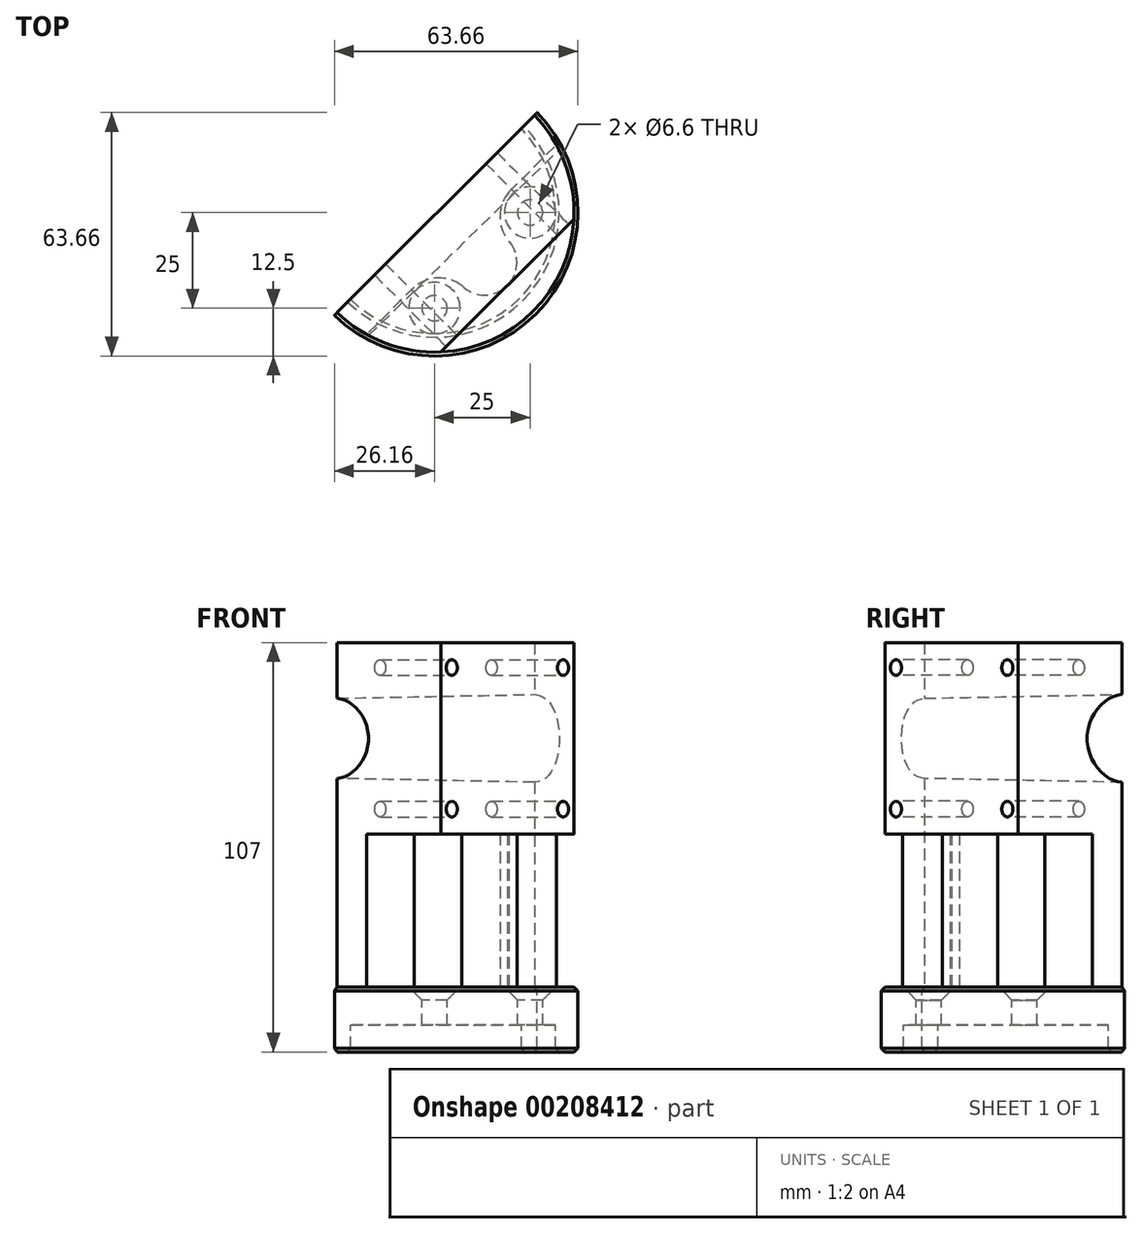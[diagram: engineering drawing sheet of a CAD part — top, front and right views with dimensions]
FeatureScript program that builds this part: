
annotation { "Feature Type Name" : "Feature", "Feature Type Description" : "" }
export const myFeature = defineFeature(function(context is Context, id is Id, definition is map)
    precondition{}
    {
        {
            var Q0;
            Q0=qCreatedBy(makeId("Front.planeOp"),FACE);
            var sketch = newSketch(context, id + "F0", { "sketchPlane" : qUnion([Q0])});
            skLineSegment(sketch, "E0", {"start": v(0, 0) * mm, "end": v(31.6, 0) * mm});
            skLineSegment(sketch, "E1", {"start": v(31.6, 0) * mm, "end": v(31.6, -7) * mm});
            skLineSegment(sketch, "E2", {"start": v(31.6, -7) * mm, "end": v(37.5, -7) * mm});
            skLineSegment(sketch, "E3", {"start": v(37.5, -7) * mm, "end": v(37.5, 10) * mm});
            skLineSegment(sketch, "E4", {"start": v(37.5, 10) * mm, "end": v(0, 10) * mm});
            skLineSegment(sketch, "E5", {"start": v(0, 10) * mm, "end": v(0, 0) * mm});
            skSolve(sketch);
        }
        {
            var Q0;
            Q0=qSketchRegion(id+"F0",true);
            var Q1;
            Q1=sQuery(id+"F0.wireOp",EDGE,"E5");
            revolve(context, id + "F1", {"entities" : qUnion([Q0]), "axis" : qUnion([Q1]), "revolveType" : RevolveType.TWO_DIRECTIONS, "angle" : 135 * degree, "angleBack" : 315 * degree});
        }
        {
            var Q0;
            Q0=makeQuery(id+"F1.opRevolve","SWEPT_EDGE",EDGE,{"disambiguationData":[OSD([sQuery(id+"F0.wireOp",EDGE,"E1"),sQuery(id+"F0.wireOp",EDGE,"E2")])]});
            var Q1;
            Q1=makeQuery(id+"F1.opRevolve","SWEPT_EDGE",EDGE,{"disambiguationData":[OSD([sQuery(id+"F0.wireOp",EDGE,"E2"),sQuery(id+"F0.wireOp",EDGE,"E3")])]});
            var Q2;
            Q2=makeQuery(id+"F1.opRevolve","SWEPT_EDGE",EDGE,{"disambiguationData":[OSD([sQuery(id+"F0.wireOp",EDGE,"E3"),sQuery(id+"F0.wireOp",EDGE,"E4")])]});
            chamfer(context, id + "F2", {"entities" : qUnion([Q0, Q1, Q2]), "width" : 1 * mm, "tangentPropagation" : true});
        }
        {
            var Q0;
            Q0=makeQuery(id+"F1.opRevolve","SWEPT_FACE",FACE,{"disambiguationData":[OSD([sQuery(id+"F0.wireOp",EDGE,"E4")])]});
            var sketch = newSketch(context, id + "F3", { "sketchPlane" : qUnion([Q0])});
            skCircle(sketch, "E6", {"center": v(0, 0) * mm, "radius": 25 * mm, "construction": true});
            skPoint(sketch, "E7", {"position": v(25, 0) * mm});
            skPoint(sketch, "E8", {"position": v(0, -25) * mm});
            skSolve(sketch);
        }
        {
            var Q0;
            Q0=sQuery(id+"F3.wireOp",VERTEX,"06cf2421-47d0-4dc6-992a-3eddbef67247");
            var Q1;
            Q1=sQuery(id+"F3.wireOp",VERTEX,"E7");
            var Q2;
            Q2=sQuery(id+"F3.wireOp",VERTEX,"E8");
            var Q3;
            Q3=sQuery(id+"F3.wireOp",VERTEX,"fbc0e9e7-8500-45a9-a549-826aceaf9aa4");
            var Q4;
            Q4=makeQuery(id+"F1.opRevolve","SWEPT_BODY",BODY,{"disambiguationData":[OSD([sQuery(id+"F0.wireOp",EDGE,"E0"),sQuery(id+"F0.wireOp",EDGE,"E1"),sQuery(id+"F0.wireOp",EDGE,"E2"),sQuery(id+"F0.wireOp",EDGE,"E3"),sQuery(id+"F0.wireOp",EDGE,"E4"),sQuery(id+"F0.wireOp",EDGE,"E5")])]});
            hole(context, id + "F4", {"style" : HoleStyle.C_SINK, "endStyle" : HoleEndStyle.THROUGH, "standardTappedOrClearance" : lookupTablePath({ "standard" : "ISO", "fit" : "Normal", "size" : "M6", "type" : "Clearance" }), "standardBlindInLast" : lookupTablePath({ "fit" : "Standard", "standard" : "ISO", "size" : "M6", "type" : "Clearance" }), "holeDiameter" : 6.6 * mm, "cSinkDiameter" : 13.44 * mm, "cSinkAngle" : 90 * degree, "locations" : qUnion([Q0, Q1, Q2, Q3]), "scope" : qUnion([Q4]), "isTappedThrough" : true});
        }
        {
            var Q0;
            Q0=makeQuery(id+"F1.opRevolve","SWEPT_FACE",FACE,{"disambiguationData":[OSD([sQuery(id+"F0.wireOp",EDGE,"E4")])]});
            var sketch = newSketch(context, id + "F5", { "sketchPlane" : qUnion([Q0])});
            skLineSegment(sketch, "E9", {"start": v(0, 0) * mm, "end": v(7.07, -7.07) * mm});
            skLineSegment(sketch, "E10", {"start": v(7.07, -7.07) * mm, "end": v(31.9, 17.75) * mm});
            skLineSegment(sketch, "E11", {"start": v(7.07, -7.07) * mm, "end": v(-17.75, -31.9) * mm});
            skLineSegment(sketch, "E12.bottom", {"start": v(7.07, -7.07) * mm, "end": v(19.07, -7.07) * mm, "construction": true});
            skLineSegment(sketch, "E12.top", {"start": v(7.07, -19.07) * mm, "end": v(19.07, -19.07) * mm, "construction": true});
            skLineSegment(sketch, "E12.left", {"start": v(7.07, -7.07) * mm, "end": v(7.07, -19.07) * mm, "construction": true});
            skLineSegment(sketch, "E12.right", {"start": v(19.07, -7.07) * mm, "end": v(19.07, -19.07) * mm, "construction": true});
            skArc(sketch, "E13", {"start": v(7.07, -19.07) * mm, "mid": v(0.8, -17.12) * mm, "end": v(-5.34, -19.48) * mm});
            skArc(sketch, "E14", {"start": v(19.48, 5.34) * mm, "mid": v(17.12, -0.8) * mm, "end": v(19.07, -7.07) * mm});
            skArc(sketch, "E15", {"start": v(7.07, -19.07) * mm, "mid": v(19.07, -19.07) * mm, "end": v(19.07, -7.07) * mm});
            skSolve(sketch);
        }
        {
            var Q0;
            Q0=qSketchRegion(id+"F5",true);
            var Q1;
            {var subQ7=sQuery(id+"F5.wireOp",EDGE,"E9");Q1=makeQuery(id+"F5.imprint","IMPRINT",FACE,{"disambiguationData":[TD([[makeQuery(id+"F5.imprint","IMPRINT",EDGE,{"derivedFrom":subQ7}),-1.0]])]});}
            var Q2;
            {var subQ6=sQuery(id+"F5.wireOp",EDGE,"E9");Q2=makeQuery(id+"F5.imprint","IMPRINT",FACE,{"disambiguationData":[TD([[makeQuery(id+"F5.imprint","IMPRINT",EDGE,{"derivedFrom":subQ6}),1.0]])]});}
            extrude(context, id + "F6", {"entities" : qUnion([Q0, Q1, Q2]), "operationType" : NewBodyOperationType.ADD, "depth" : 40 * mm});
        }
        {
            var Q0;
            Q0=makeQuery(id+"F6.opExtrude","CAP_FACE",FACE,{"disambiguationData":[OSD([sQuery(id+"F0.wireOp",EDGE,"E3"),sQuery(id+"F0.wireOp",EDGE,"E4"),sQuery(id+"F5.wireOp",EDGE,"E10"),sQuery(id+"F5.wireOp",EDGE,"E11"),sQuery(id+"F5.wireOp",EDGE,"E13"),sQuery(id+"F5.wireOp",EDGE,"E14"),sQuery(id+"F5.wireOp",EDGE,"E15")])],"isStart":false});
            var sketch = newSketch(context, id + "F7", { "sketchPlane" : qUnion([Q0])});
            skArc(sketch, "E16", {"start": v(25.8, 25.8) * mm, "mid": v(25.8, -25.8) * mm, "end": v(-25.8, -25.8) * mm});
            skLineSegment(sketch, "E17", {"start": v(-25.8, -25.8) * mm, "end": v(25.8, 25.8) * mm});
            skLineSegment(sketch, "E18", {"start": v(19.07, -19.07) * mm, "end": v(36.46, -1.68) * mm});
            skLineSegment(sketch, "E19", {"start": v(36.46, -1.68) * mm, "end": v(1.68, -36.46) * mm});
            skSolve(sketch);
        }
        {
            var Q0;
            {var subQ1=makeQuery(id+"F6.opExtrude","CAP_EDGE",EDGE,{"disambiguationData":[OSD([sQuery(id+"F5.wireOp",EDGE,"E10")])],"isStart":false});Q0=makeQuery(id+"F7.imprint","IMPRINT",FACE,{"disambiguationData":[TD([[makeQuery(id+"F7.imprint","IMPRINT",EDGE,{"derivedFrom":subQ1}),-1.0]])]});}
            var Q1;
            {var subQ1=makeQuery(id+"F6.opExtrude","CAP_EDGE",EDGE,{"disambiguationData":[OSD([sQuery(id+"F5.wireOp",EDGE,"E11")])],"isStart":false});Q1=makeQuery(id+"F7.imprint","IMPRINT",FACE,{"disambiguationData":[TD([[makeQuery(id+"F7.imprint","IMPRINT",EDGE,{"derivedFrom":subQ1}),1.0]])]});}
            var Q2;
            {var subQ0=sQuery(id+"F7.wireOp",EDGE,"E17");Q2=makeQuery(id+"F7.imprint","IMPRINT",FACE,{"disambiguationData":[TD([[makeQuery(id+"F7.imprint","IMPRINT",EDGE,{"derivedFrom":subQ0}),-1.0]])]});}
            extrude(context, id + "F8", {"entities" : qUnion([Q0, Q1, Q2]), "operationType" : NewBodyOperationType.ADD, "depth" : 50 * mm});
        }
        {
            var Q0;
            {var subQ0=sQuery(id+"F0.wireOp",EDGE,"E4");Q0=makeQuery(id+"F8.boolean.opBoolean","MERGE",FACE,{"derivedFrom":[makeQuery(id+"F6.boolean.opBoolean","MERGE",FACE,{"derivedFrom":[makeQuery(id+"F1.opRevolve","CAP_FACE",FACE,{"disambiguationData":[OSD([sQuery(id+"F0.wireOp",EDGE,"E0"),sQuery(id+"F0.wireOp",EDGE,"E1"),sQuery(id+"F0.wireOp",EDGE,"E2"),sQuery(id+"F0.wireOp",EDGE,"E3"),subQ0,sQuery(id+"F0.wireOp",EDGE,"E5")])],"isStart":true}),makeQuery(id+"F6.opExtrude","SWEPT_FACE",FACE,{"disambiguationData":[OSD([subQ0])]})]}),makeQuery(id+"F8.opExtrude","SWEPT_FACE",FACE,{"disambiguationData":[OSD([sQuery(id+"F7.wireOp",EDGE,"E17")])]})]});}
            var sketch = newSketch(context, id + "F9", { "sketchPlane" : qUnion([Q0])});
            skLineSegment(sketch, "E20", {"start": v(-36.5, 100) * mm, "end": v(-36.5, 86.5) * mm, "construction": true});
            skLineSegment(sketch, "E21", {"start": v(36.5, 100) * mm, "end": v(36.5, 85.5) * mm, "construction": true});
            skLineSegment(sketch, "E22", {"start": v(-36.5, 86.5) * mm, "end": v(-36.5, 63.5) * mm, "construction": true});
            skLineSegment(sketch, "E23", {"start": v(36.5, 85.5) * mm, "end": v(36.5, 64.5) * mm, "construction": true});
            skLineSegment(sketch, "E24", {"start": v(-36.5, 86.5) * mm, "end": v(36.5, 85.5) * mm});
            skLineSegment(sketch, "E25", {"start": v(36.5, 85.5) * mm, "end": v(36.5, 64.5) * mm});
            skLineSegment(sketch, "E26", {"start": v(36.5, 64.5) * mm, "end": v(-36.5, 63.5) * mm});
            skLineSegment(sketch, "E27", {"start": v(-36.5, 63.5) * mm, "end": v(-36.5, 86.5) * mm});
            skLineSegment(sketch, "E28", {"start": v(-36.5, 75) * mm, "end": v(36.5, 75) * mm});
            skSolve(sketch);
        }
        {
            var Q0;
            {var subQ0=sQuery(id+"F9.wireOp",EDGE,"E24");Q0=makeQuery(id+"F9.imprint","IMPRINT",FACE,{"disambiguationData":[TD([[makeQuery(id+"F9.imprint","IMPRINT",EDGE,{"derivedFrom":subQ0}),-1.0]])]});}
            var Q1;
            Q1=sQuery(id+"F9.wireOp",EDGE,"E28");
            revolve(context, id + "F10", {"operationType" : NewBodyOperationType.REMOVE, "entities" : qUnion([Q0]), "axis" : qUnion([Q1]), "revolveType" : RevolveType.FULL, "oppositeDirection" : true});
        }
        {
            var Q0;
            Q0=makeQuery(id+"F8.opExtrude","SWEPT_FACE",FACE,{"disambiguationData":[OSD([sQuery(id+"F7.wireOp",EDGE,"E19")])]});
            var sketch = newSketch(context, id + "F11", { "sketchPlane" : qUnion([Q0])});
            skLineSegment(sketch, "E29", {"start": v(24.6, 100) * mm, "end": v(24.6, 93.5) * mm, "construction": true});
            skLineSegment(sketch, "E30", {"start": v(24.6, 93.5) * mm, "end": v(20.6, 93.5) * mm, "construction": true});
            skLineSegment(sketch, "E31", {"start": v(-24.6, 100) * mm, "end": v(-24.6, 93.5) * mm, "construction": true});
            skLineSegment(sketch, "E32", {"start": v(-24.6, 93.5) * mm, "end": v(-20.6, 93.5) * mm, "construction": true});
            skLineSegment(sketch, "E33", {"start": v(-24.6, 50) * mm, "end": v(-24.6, 56.5) * mm, "construction": true});
            skLineSegment(sketch, "E34", {"start": v(-24.6, 56.5) * mm, "end": v(-20.6, 56.5) * mm, "construction": true});
            skLineSegment(sketch, "E35", {"start": v(24.6, 50) * mm, "end": v(24.6, 56.5) * mm, "construction": true});
            skLineSegment(sketch, "E36", {"start": v(24.6, 56.5) * mm, "end": v(20.6, 56.5) * mm, "construction": true});
            skPoint(sketch, "E37", {"position": v(-20.6, 93.5) * mm});
            skPoint(sketch, "E38", {"position": v(20.6, 93.5) * mm});
            skPoint(sketch, "E39", {"position": v(20.6, 56.5) * mm});
            skPoint(sketch, "E40", {"position": v(-20.6, 56.5) * mm});
            skSolve(sketch);
        }
        {
            var Q0;
            Q0=sQuery(id+"F11.wireOp",VERTEX,"E38");
            var Q1;
            Q1=sQuery(id+"F11.wireOp",VERTEX,"E39");
            var Q2;
            Q2=sQuery(id+"F11.wireOp",VERTEX,"E40");
            var Q3;
            Q3=sQuery(id+"F11.wireOp",VERTEX,"E37");
            var Q4;
            Q4=makeQuery(id+"F1.opRevolve","SWEPT_BODY",BODY,{"disambiguationData":[OSD([sQuery(id+"F0.wireOp",EDGE,"E0"),sQuery(id+"F0.wireOp",EDGE,"E1"),sQuery(id+"F0.wireOp",EDGE,"E2"),sQuery(id+"F0.wireOp",EDGE,"E3"),sQuery(id+"F0.wireOp",EDGE,"E4"),sQuery(id+"F0.wireOp",EDGE,"E5")])]});
            hole(context, id + "F12", {"style" : HoleStyle.SIMPLE, "endStyle" : HoleEndStyle.THROUGH, "standardTappedOrClearance" : lookupTablePath({ "standard" : "ISO", "engagement" : "75%", "pitch" : "0.9 mm", "size" : "M5", "type" : "Tapped" }), "standardBlindInLast" : lookupTablePath({ "standard" : "ISO", "engagement" : "75%", "pitch" : "0.9 mm", "size" : "M5", "type" : "Tapped" }), "holeDiameter" : 4.1 * mm, "startFromSketch" : true, "locations" : qUnion([Q0, Q1, Q2, Q3]), "scope" : qUnion([Q4]), "isTappedThrough" : true, "showTappedDepth" : true});
        }
        {
            var Q0;
            {var subQ0=sQuery(id+"F0.wireOp",EDGE,"E4");var subQ1=sQuery(id+"F0.wireOp",EDGE,"E3");var subQ2=sQuery(id+"F7.wireOp",EDGE,"E17");var subQ7=sQuery(id+"F0.wireOp",EDGE,"E2");var subQ8=sQuery(id+"F0.wireOp",EDGE,"E1");var subQ9=sQuery(id+"F0.wireOp",EDGE,"E0");Q0=makeQuery(id+"F10.boolean.opBoolean","SPLIT",FACE,{"disambiguationData":[TD([makeQuery(id+"F1.opRevolve","SWEPT_FACE",FACE,{"disambiguationData":[OSD([subQ9])]})])],"derivedFrom":makeQuery(id+"F8.boolean.opBoolean","MERGE",FACE,{"derivedFrom":[makeQuery(id+"F6.boolean.opBoolean","MERGE",FACE,{"derivedFrom":[makeQuery(id+"F1.opRevolve","CAP_FACE",FACE,{"disambiguationData":[OSD([subQ9,subQ8,subQ7,subQ1,subQ0,sQuery(id+"F0.wireOp",EDGE,"E5")])],"isStart":true}),makeQuery(id+"F6.opExtrude","SWEPT_FACE",FACE,{"disambiguationData":[OSD([subQ0])]})]}),makeQuery(id+"F8.opExtrude","SWEPT_FACE",FACE,{"disambiguationData":[OSD([subQ2])]})]})});}
            var sketch = newSketch(context, id + "F13", { "sketchPlane" : qUnion([Q0])});
            skLineSegment(sketch, "E41.bottom", {"start": v(48.37, 113.56) * mm, "end": v(-52.25, 113.56) * mm});
            skLineSegment(sketch, "E41.top", {"start": v(48.37, -38.1) * mm, "end": v(-52.25, -38.1) * mm});
            skLineSegment(sketch, "E41.left", {"start": v(48.37, 113.56) * mm, "end": v(48.37, -38.1) * mm});
            skLineSegment(sketch, "E41.right", {"start": v(-52.25, 113.56) * mm, "end": v(-52.25, -38.1) * mm});
            skSolve(sketch);
        }
        {
            var Q0;
            Q0=qSketchRegion(id+"F13",true);
            extrude(context, id + "F14", {"entities" : qUnion([Q0]), "operationType" : NewBodyOperationType.REMOVE, "oppositeDirection" : true, "depth" : .5 * mm});
        }
    });
